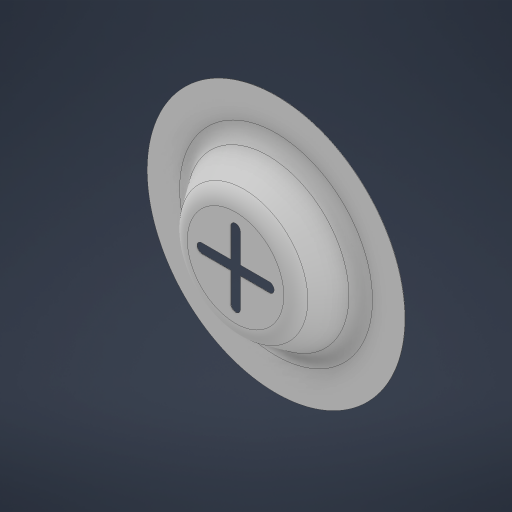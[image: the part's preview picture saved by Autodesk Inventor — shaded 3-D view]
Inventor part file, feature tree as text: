
AUTODESK INVENTOR PART (.ipt)
format: ipt  version: 2024.3 (Build 283343010, 343A)  size: 260,608 bytes
history: native  units: mm
features: sketch x2, revolve x1, extrude x1
ambient origin geometry x8: Origin, YZ Plane, XZ Plane, XY Plane, X Axis, Y Axis, Z Axis, Center Point
bodies: Volumenkörper1 (feature_tree)
feature tree (4):
  revolve  "Umdrehung1"
  extrude  "Extrusion1"  Depth=10.0mm
  sketch  "Skizze1"  dims[d0=0.02mm d2=10.0mm]
  sketch  "Skizze2"  dims[d3=0.02mm d4=1.0mm d5=2.1mm d6=5.0mm d7=90.0deg d8=4.0mm d9=0.5mm d10=40.0mm d12=360.0deg d14=0.0mm d15=0.0mm]
